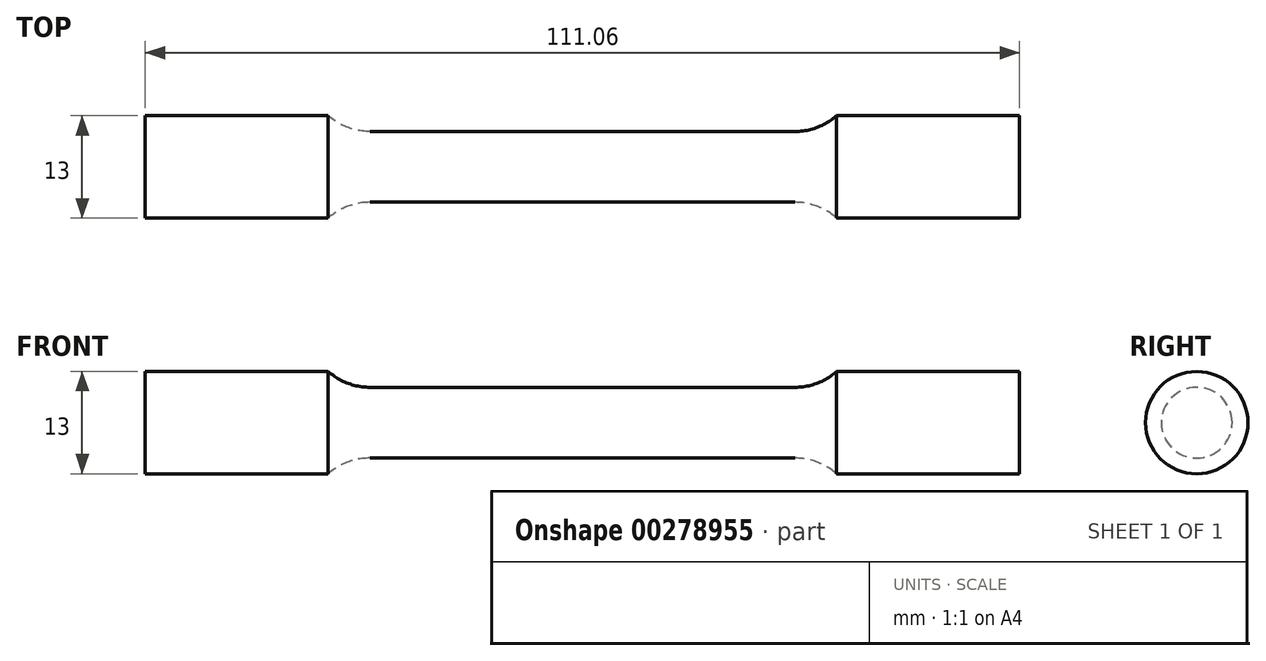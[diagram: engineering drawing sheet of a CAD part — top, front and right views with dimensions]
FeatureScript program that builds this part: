
annotation { "Feature Type Name" : "Feature", "Feature Type Description" : "" }
export const myFeature = defineFeature(function(context is Context, id is Id, definition is map)
    precondition{}
    {
        {
            var Q0;
            Q0=qCreatedBy(makeId("Front.planeOp"),FACE);
            var sketch = newSketch(context, id + "F0", { "sketchPlane" : qUnion([Q0])});
            skLineSegment(sketch, "E0", {"start": v(0, 4.5) * mm, "end": v(27, 4.5) * mm});
            skArc(sketch, "E1", {"start": v(27, 4.5) * mm, "mid": v(29.83, 5.02) * mm, "end": v(32.3, 6.5) * mm});
            skLineSegment(sketch, "E2", {"start": v(32.3, 6.5) * mm, "end": v(55.53, 6.5) * mm});
            skLineSegment(sketch, "E3", {"start": v(55.53, 6.5) * mm, "end": v(55.53, 0) * mm});
            skLineSegment(sketch, "E4.MirrorCS", {"start": v(0, 4.5) * mm, "end": v(-27, 4.5) * mm});
            skLineSegment(sketch, "E5.MirrorCS", {"start": v(-55.53, 6.5) * mm, "end": v(-55.53, 0) * mm});
            skLineSegment(sketch, "E6.MirrorCS", {"start": v(-32.3, 6.5) * mm, "end": v(-55.53, 6.5) * mm});
            skArc(sketch, "E7.MirrorCS", {"start": v(-27, 4.5) * mm, "mid": v(-29.83, 5.02) * mm, "end": v(-32.3, 6.5) * mm});
            skLineSegment(sketch, "E8", {"start": v(-55.53, 0) * mm, "end": v(55.53, 0) * mm});
            skSolve(sketch);
        }
        {
            var Q0;
            Q0 = qSketchRegion(id + "F0", true);
            var Q1;
            Q1=sQuery(id+"F0.wireOp",EDGE,"E8");
            revolve(context, id + "F1", {"entities" : qUnion([Q0]), "axis" : qUnion([Q1]), "revolveType" : RevolveType.FULL});
        }
    });
